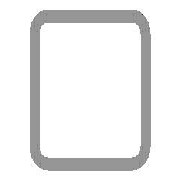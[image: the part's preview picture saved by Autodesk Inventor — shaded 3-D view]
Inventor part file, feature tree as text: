
AUTODESK INVENTOR PART (.ipt)
format: ipt  version: 2021 (Build 250183000, 183)  size: 127,488 bytes
history: native  units: mm (DEFAULTED — no unit token found)
features: other x3, sketch x3, extrude x1, plane x1
ambient origin geometry x8: Origin, YZ Plane, XZ Plane, XY Plane, X Axis, Y Axis, Z Axis, Center Point
bodies: Solid1 (feature_tree)
feature tree (8):
  other  "Driven Length"
  other  "Płaszczyzna początkowa"
  other  "Płaszczyzna końcowa"
  extrude  "Bryła"  TaperAngle=0.0deg  [1 undecoded]
  sketch  "Szkic"
  sketch  "Sketch3"  dims[d3=2000.0mm d4=0.0mm]
  plane  "Work Plane3"
  sketch  "Sketch4"  dims[d7=4.0mm d9=20.0mm d11=20.0mm d12=2.0mm d13=-0.0mm d14=2000.0mm d15=10.0mm d16=10.0mm d17=90.0deg d18=2000.0mm]
note: 1 required parameter value undecoded (feature->parameter linkage not recoverable at this tier; creation-order binding heuristic only, values carry confidence <= 0.55)
